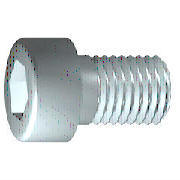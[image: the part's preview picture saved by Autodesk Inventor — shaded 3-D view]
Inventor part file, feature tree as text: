
AUTODESK INVENTOR PART (.ipt)
format: ipt  version: 2016 (Build 200138000, 138)  size: 184,320 bytes
history: native  units: mm (DEFAULTED — no unit token found)
features: sketch x2, other x1, extrude x1, plane x1, fillet x1
ambient origin geometry x7: Origin, YZ Plane, XY Plane, X Axis, Y Axis, Z Axis, Center Point
bodies: Solid1 (feature_tree)
feature tree (6):
  other  "Körper"
  extrude  "Loch"  Depth=3.0mm
  plane  "Work Plane1"
  fillet  "Fillet2"  Radius=3.0mm
  sketch  "Skizze1"  dims[d1=18.0mm d2=0.306825mm d3=3.0mm]
  sketch  "Skizze2"  dims[d4=1.3mm d5=60.0deg d6=3.0mm d7=3.0mm d8=2.886751mm d9=5.5mm d10=90.0deg d11=10.0mm d12=0.0mm d13=18.0mm d14=0.0mm d15=0.306725mm d16=0.306725mm d17=0.3mm d19=0.0mm d26=25.0mm d27=45.0deg d28=0.0mm d29=0.0mm d30=0.1mm]
